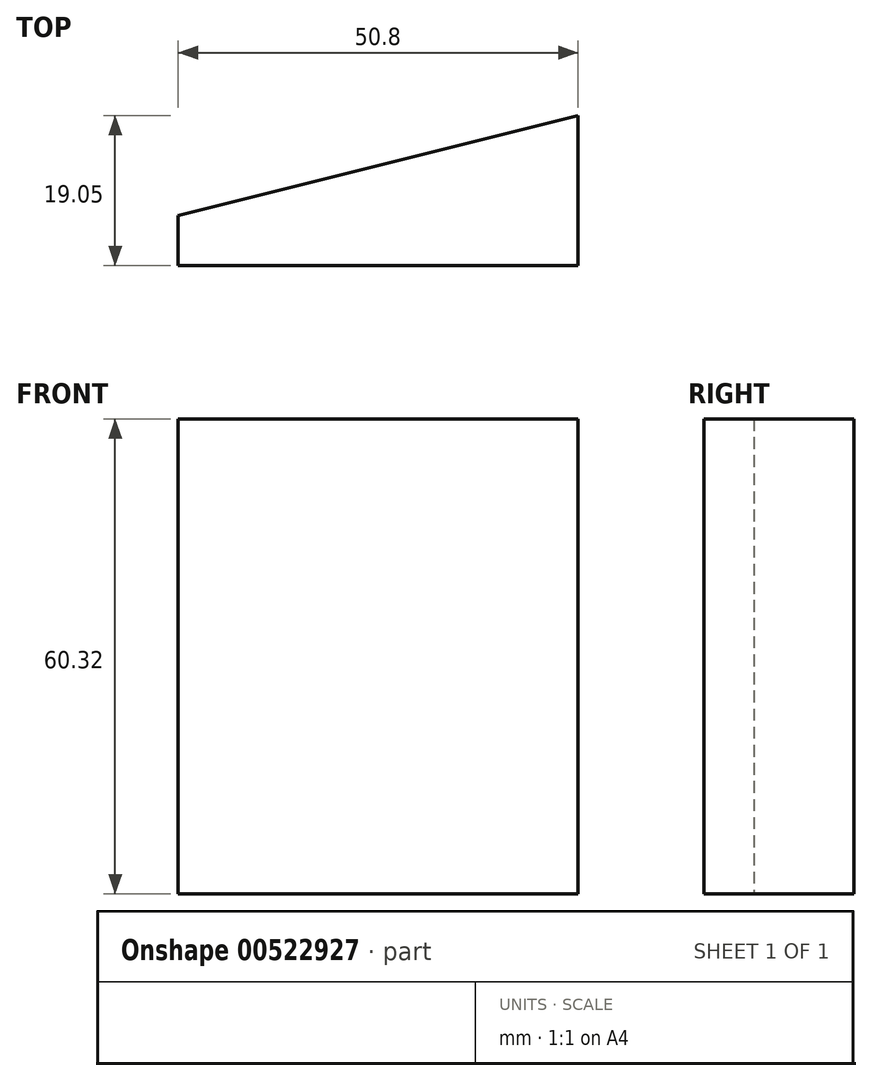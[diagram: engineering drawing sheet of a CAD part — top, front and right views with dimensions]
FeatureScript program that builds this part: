
annotation { "Feature Type Name" : "Feature", "Feature Type Description" : "" }
export const myFeature = defineFeature(function(context is Context, id is Id, definition is map)
    precondition{}
    {
        {
            var Q0;
            Q0=qCreatedBy(makeId("Top.planeOp"),FACE);
            var sketch = newSketch(context, id + "F0", { "sketchPlane" : qUnion([Q0])});
            skLineSegment(sketch, "E0", {"start": v(-30.08, 0) * mm, "end": v(-30.08, 6.35) * mm});
            skLineSegment(sketch, "E1", {"start": v(-30.08, 6.35) * mm, "end": v(20.72, 19.05) * mm});
            skLineSegment(sketch, "E2", {"start": v(20.72, 19.05) * mm, "end": v(20.72, 0) * mm});
            skLineSegment(sketch, "E3", {"start": v(20.72, 0) * mm, "end": v(-30.08, 0) * mm});
            skSolve(sketch);
        }
        {
            var Q0;
            Q0=makeQuery(id+"F0.imprint","IMPRINT",FACE,{"disambiguationData":[TD([[makeQuery(id+"F0.imprint","IMPRINT",EDGE,{"derivedFrom":sQuery(id+"F0.wireOp",EDGE,"E0")}),-1.0]])]});
            extrude(context, id + "F1", {"entities" : qUnion([Q0]), "depth" : 60.32 * mm, "offsetDistance" : 25.4 * mm});
        }
    });
